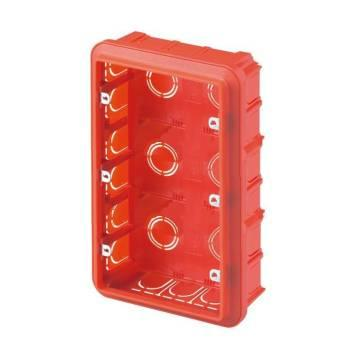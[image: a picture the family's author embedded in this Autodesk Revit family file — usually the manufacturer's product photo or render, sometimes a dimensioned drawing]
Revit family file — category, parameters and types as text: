
# Revit family: Building-FlushMountingEnclosures-GEWISS-24SC-BOXES_BIGBOX_6P+6P+6P
name_source: partatom
category: Apparecchi elettrici
revit_build: Autodesk Revit 2016 (Build: 20161004_0715(x64)
units: mm (PartAtom-declared; Revit-internal decimal feet)

## family parameters
Condiviso = Sì
Host = Superficie
Mantenere orientamento annotazione = Sì
Numero OmniClass = 23.80.30.14.24
Punto di calcolo locali = Sì
Quota connettore circolare = Usa diametro
Taglio con vuoti quando caricato = Sì
Tipo di parte = Normale
Titolo OmniClass = Junction Boxes

## types (1)
- GW24239 - Box 18P (6+6+6)
    Catalogue = BUILDING
    Catalogue Range = 24SC
    Centro viti = 107 mm  [stored 0.35105 ft]
    Characteristics = Halogen free
    Compartment pre-arrangement = 3
    Description: = 18 gang (6+6+6)
    Descrizione = 18 GANG F.M. BOX W.METAL FIXING SUPP.
    EAN code = 8011564025004
    Electrocod = 0110
    Fixing supports axles distance = 163,5MM
    For walls = Masonry
    Glow Wire Test = 650°C
    IDF = f4778d46-67a2-40a8-8bc7-7530a1416b7a
    IDT = ae64a0fb-03f4-4e53-89b4-0a5e4ee210f3
    Immagine tipo = GW24239.jpg
    Installation = Flush mounting enclosures
    Modello = GW24239
    No. SYSTEM modules = 18 gang (6+6+6)
    Operating temperature = -15 ÷ +60°C
    Outer dim. LxHxD (mm) = 186x190x65
    Produttore = GEWISS S.p.A.
    Prospetto di default = 45 mm  [stored 0.147638 ft]
    SEO = Box
    Technical sheet = https://www.gewiss.com
    Thermo-pressure with ball = 70
    Type of material = Halogen-free in compliance with EN 60754-2
    Type: = High capacity
    URL = https://www.gewiss.com
    Version file RFA = 19.0

note: source unit labels omitted for Thermo-pressure with ball — the stored unit's dimension contradicts the parameter name (converter mislabeling)

note: [stored X ft] marks values corroborated as IEEE doubles in the binary element streams (Revit-internal decimal feet)
